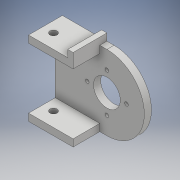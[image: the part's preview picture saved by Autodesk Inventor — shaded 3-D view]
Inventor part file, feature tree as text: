
AUTODESK INVENTOR PART (.ipt)
format: ipt  version: 2018 (Build 220112000, 112)  size: 159,744 bytes
history: native  units: mm
features: extrude x3, hole x3, sketch x3, fillet x1, pattern_circular x1
ambient origin geometry x8: Origin, YZ Plane, XZ Plane, XY Plane, X Axis, Y Axis, Z Axis, Center Point
bodies: Solid1 (feature_tree)
feature tree (11):
  extrude  "Extrusion1"  Depth=4.0mm
  extrude  "Extrusion2"  Depth=42.0mm
  fillet  "Fillet1"  Radius=50.0mm
  hole  "Hole1"  [1 undecoded]
  hole  "Hole2"  [1 undecoded]
  hole  "Hole6"  [1 undecoded]
  pattern_circular  "Circular Pattern1"  [2 undecoded]
  extrude  "Extrusion3"  Depth=4.0mm TaperAngle=360.0deg
  sketch  "Sketch1"  dims[d0=4.0mm d1=4.0mm]
  sketch  "Sketch2"  dims[d2=15.0mm d3=42.0mm d4=50.0mm d5=0.0mm]
  sketch  "Sketch3"  dims[d6=15.0mm d7=25.0mm d8=50.0mm d9=0.0mm d10=21.0mm d11=10.0mm d12=10.0mm d13=15.0mm d14=6.0mm d15=4.0mm d16=2.0mm d17=90.0deg d18=8.0mm d19=20.594885mm d20=10.0mm d69=29.0mm d22=2.0mm d23=6.0mm d24=4.0mm d25=2.0mm d26=90.0deg d27=8.0mm d28=20.594885mm d56=6.0mm d70=8.0mm d58=4.0mm d59=6.0mm d60=4.0mm d61=2.0mm d62=90.0deg d63=42.0mm d64=0.0mm d65=40.0mm d66=360.0deg d68=3.0mm d71=4.0mm d72=0.0mm]
note: 5 required parameter values undecoded (feature->parameter linkage not recoverable at this tier; creation-order binding heuristic only, values carry confidence <= 0.55)
